# Revit family: HVAC_Fireplaces_Regency-Fireplace_New-York-gas-fireplace_CV40E
name_source: partatom
category: Specialty Equipment
units: mm (PartAtom-declared; Revit-internal decimal feet)

## family parameters
Classification Number = 23.40.20.34.14
Cut with Voids When Loaded = No
Enable Cutting in Views = No
Host = Face
Maintain Annotation Orientation = No
Part Type = Normal
Room Calculation Point = No
Round Connector Dimension = Use Diameter
Shared = No

## types (2) — shared parameters
Apparent Load = 0 VA
Current = 2 A
Depth = 19 "
Description = The Regency City Series New York View linear gas fireplaces feature a seamless clear view of the fire with the ability to be integrated into any décor style.
Duct Connector Description = 4” Inner / 6-5/8” Outer
Duct Diameter = 8 "
Frequency = 60 Hz
Gas flow = 0.0 L/s
Height = 31 "
Housing Material = Regency Fireplace - Metal - Black
Manufacturer = Regency Fireplace
Minimum Input Altitude 0-4500 ft. (0-1372m) = 15,500 Btu/h (4.54 kW)
Number of Poles = 1
OCTF Material = Regency Fireplace - Metal - Black
Panel Material = Regency Fireplace - Metal - Black
Pipe Diameter = 1 "
Power Consumption = 0 W
Power Factor = 1
Product Documentation Link = https://assets.regency-fire.com
Product Page URL = https://www.regency-fire.com
Product data url = https://www.bimobject.com
URL = https://www.regency-fire.com
Ventilation flow = 0.0 L/s
Visible connector = No
Voltage = 120 V
WIFI Dongle Installation = Yes
Width = 43 "
zero-valued in all types: Default Elevation, Version

## per-type parameters (varying)
| type | CSA P.4.1 | Fuel Type | Gas Connector Description | Manifold Pressure - High | Manifold Pressure - Low | Maximum Input Altitude 0-4500 ft. (0-1372m) | Minimum Supply Pressure | Orifce Size -Altitude 0-4500 ft |
| CV40E-NG12 | 55.23% | Natural Gas | Natural gas supply | 3.8" WC/C.E.  (0.94 kPa) | 1.1" WC/C.E. (0.27 kPa) | 28,500 Btu/h (8.33 kW) | 5.0" WC/C.E.  (1.25 kPa) | # 42 DMS |
| CV40E-LP12 | 56.06% | Propane | Propane gas supply | 10.5" WC/C.E.  (2.62 kPa) | 2.9" WC/C.E.  (0.72 kPa) | 28,500 Btu/h (8.35kW) | 11" WC/C.E. (2.73 kPa) | # 53 DMS |

note: column(s) folded — value = type name in every type: Model

## geometry (parser evidence)
native form markers: Sweep x5
no freeform markers — native parametric forms only
